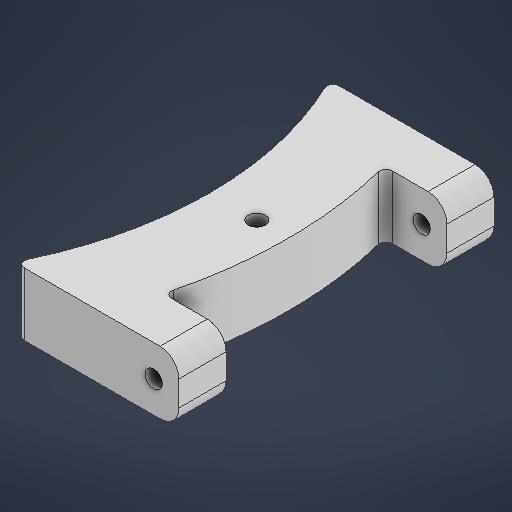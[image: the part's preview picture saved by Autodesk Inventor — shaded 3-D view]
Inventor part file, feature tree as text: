
AUTODESK INVENTOR PART (.ipt)
format: ipt  version: 2025 (Build 290162000, 162)  size: 297,472 bytes
history: native  units: in
note: dims shown in document units (in); Inventor stores cm internally (conversion verified against a paired STEP export)
features: sketch x6, fillet x4, extrude x3, hole x2, mirror x2, projected_geometry x1
ambient origin geometry x8: Origin, YZ Plane, XZ Plane, XY Plane, X Axis, Y Axis, Z Axis, Center Point
bodies: Solid1 (feature_tree)
feature tree (18):
  extrude  "Extrusion1"  Depth=8.6614in
  extrude  "Extrusion3"  Depth=3.9469in
  fillet  "Fillet1"  Radius=0.9843in
  fillet  "Fillet2"  Radius=0.5906in
  fillet  "Fillet3"  Radius=0.7874in
  hole  "Hole2"  [1 undecoded]
  mirror  "Mirror1"
  mirror  "Mirror2"
  hole  "Hole3"  [1 undecoded]
  extrude  "Extrusion7"  Depth=0.0787in
  fillet  "Fillet7"  Radius=0.3937in
  sketch  "Sketch1"  dims[d0=10.6299in d1=8.6614in]
  sketch  "Sketch4"  dims[d25=0.5906in d26=0.0in d27=0.0in]
  projected_geometry  "Projected Loop1"
  sketch  "Sketch5"  dims[d28=0.2362in d29=0.3937in]
  sketch  "Sketch7"  dims[d30=0.0787in]
  sketch  "Sketch10"  dims[d31=0.2165in d32=0.2362in d33=0.3465in d34=0.1969in d35=90.0deg d36=0.315in d37=0.8108in d38=0.315in d39=0.3937in d43=0.1969in d44=0.2362in d45=0.1575in d46=0.0787in d47=90.0deg d48=0.315in d49=0.8108in d50=5.0197in d57=0.3937in d61=0.0in d62=0.0in d63=0.0787in d68=9.8425in d74=0.2165in d75=3.937in d77=360.0deg]
  sketch  "Sketch Circular Pattern3"  dims[d2=0.7874in d3=0.0in d21=3.9469in d22=0.9843in d23=0.5906in d24=0.7874in]
note: 2 required parameter values undecoded (feature->parameter linkage not recoverable at this tier; creation-order binding heuristic only, values carry confidence <= 0.55)
